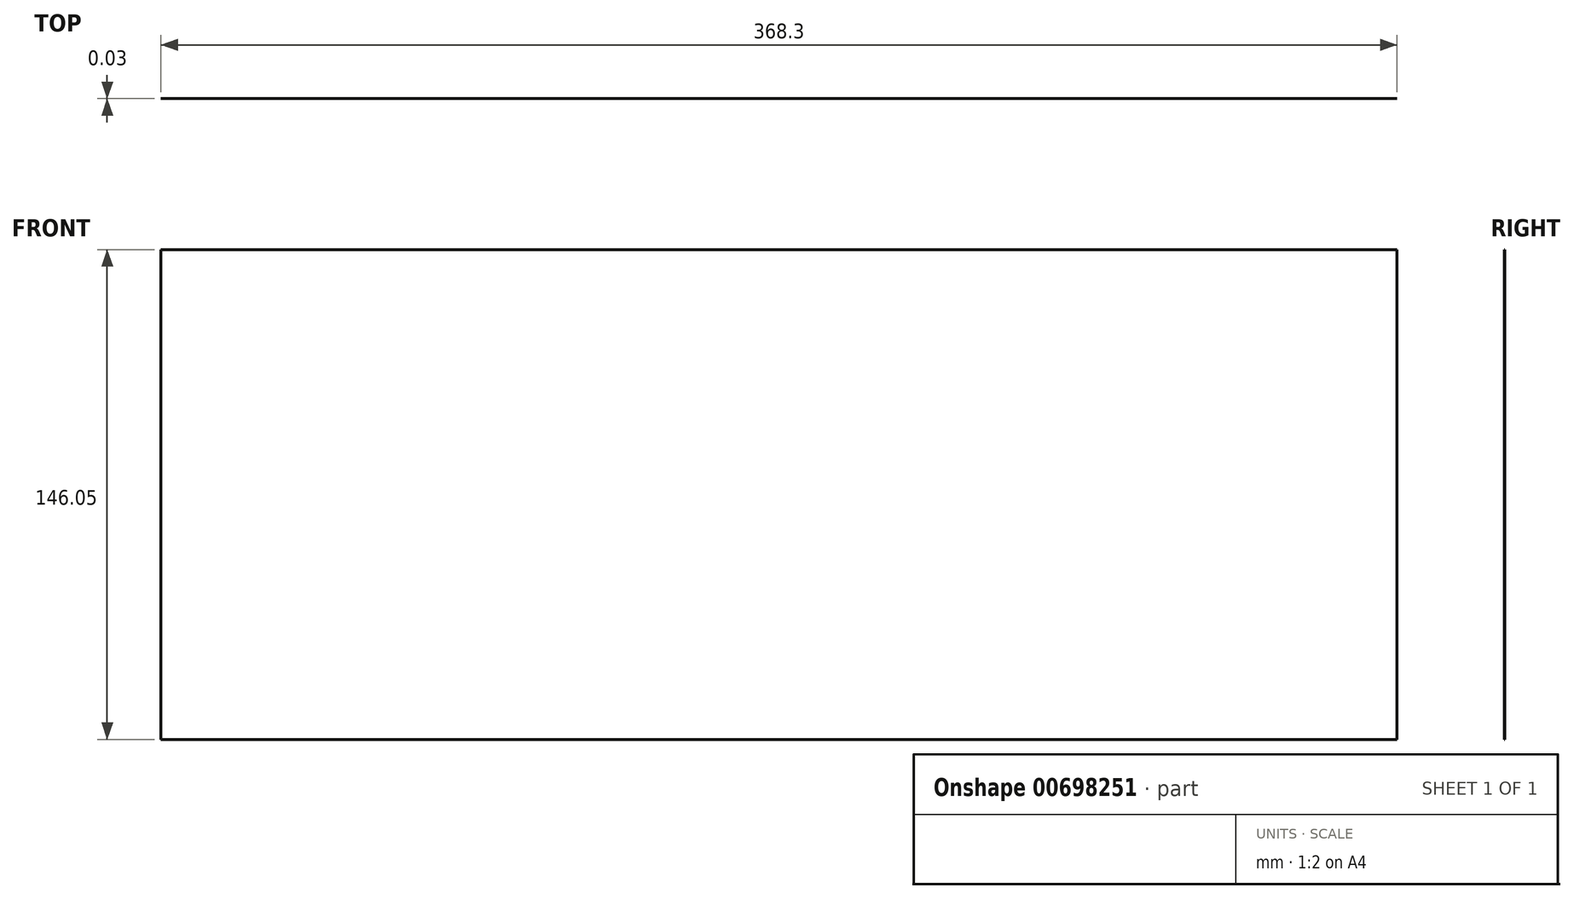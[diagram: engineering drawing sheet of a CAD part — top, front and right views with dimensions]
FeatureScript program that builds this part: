
annotation { "Feature Type Name" : "Feature", "Feature Type Description" : "" }
export const myFeature = defineFeature(function(context is Context, id is Id, definition is map)
    precondition{}
    {
        {
            var Q0;
            Q0=qCreatedBy(makeId("Front.planeOp"),FACE);
            var sketch = newSketch(context, id + "F0", { "sketchPlane" : qUnion([Q0])});
            skLineSegment(sketch, "E0.bottom", {"start": v(-183.73, -101.08) * mm, "end": v(184.57, -101.08) * mm});
            skLineSegment(sketch, "E0.top", {"start": v(-183.73, 44.97) * mm, "end": v(184.57, 44.97) * mm});
            skLineSegment(sketch, "E0.left", {"start": v(-183.73, -101.08) * mm, "end": v(-183.73, 44.97) * mm});
            skLineSegment(sketch, "E0.right", {"start": v(184.57, -101.08) * mm, "end": v(184.57, 44.97) * mm});
            skSolve(sketch);
        }
        {
            var Q0;
            Q0 = qSketchRegion(id + "F0", true);
            extrude(context, id + "F1", {"entities" : qUnion([Q0]), "depth" : 3 / 101.6 * mm, "offsetDistance" : 25.4 * mm});
        }
    });
